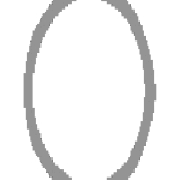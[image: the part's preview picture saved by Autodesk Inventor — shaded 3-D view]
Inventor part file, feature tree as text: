
AUTODESK INVENTOR PART (.ipt)
format: ipt  version: 2021 (Build 250183000, 183)  size: 112,128 bytes
history: native  units: in
note: dims shown in document units (in); Inventor stores cm internally (conversion verified against a paired STEP export)
features: other x4, sketch x3, plane x1
ambient origin geometry x8: Origin, YZ Plane, XZ Plane, XY Plane, X Axis, Y Axis, Z Axis, Center Point
bodies: Solid1 (feature_tree), Body (feature_tree)
feature tree (8):
  other  "Driven Length"
  other  "Frame Generator"
  other  "Start Plane"
  other  "End Plane"
  sketch  "Sketch"  dims[d2=14.625in d4=-0.0in d5=14.625in d6=0.12in d7=0.0in d8=90.0deg d9=14.625in]
  sketch  "Sketch2"  dims[d0=1.0in]
  plane  "Work Plane3"
  sketch  "Sketch3"  dims[d1=0.065in]
